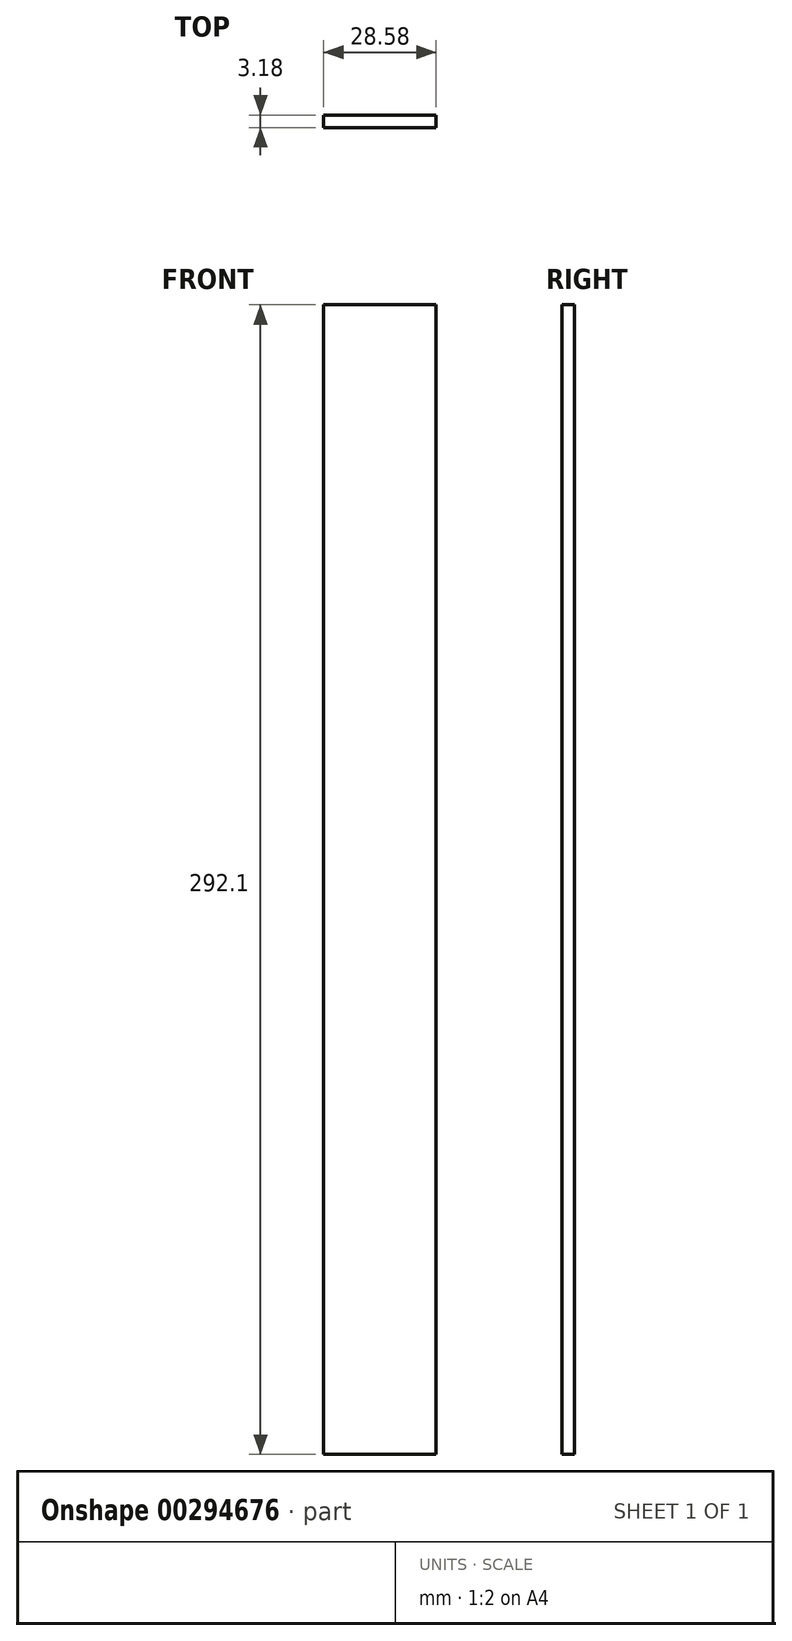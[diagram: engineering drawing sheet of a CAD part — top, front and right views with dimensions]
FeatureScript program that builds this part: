
annotation { "Feature Type Name" : "Feature", "Feature Type Description" : "" }
export const myFeature = defineFeature(function(context is Context, id is Id, definition is map)
    precondition{}
    {
        {
            var Q0;
            Q0=qCreatedBy(makeId("Front.planeOp"),FACE);
            var sketch = newSketch(context, id + "F0", { "sketchPlane" : qUnion([Q0])});
            skLineSegment(sketch, "E0.bottom", {"start": v(-14.29, 146.05) * mm, "end": v(14.29, 146.05) * mm});
            skLineSegment(sketch, "E0.top", {"start": v(-14.29, -146.05) * mm, "end": v(14.29, -146.05) * mm});
            skLineSegment(sketch, "E0.left", {"start": v(-14.29, 146.05) * mm, "end": v(-14.29, -146.05) * mm});
            skLineSegment(sketch, "E0.right", {"start": v(14.29, 146.05) * mm, "end": v(14.29, -146.05) * mm});
            skPoint(sketch, "E0.middle", {"position": v(0, 0) * mm});
            skSolve(sketch);
        }
        {
            var Q0;
            Q0=makeQuery(id+"F0.imprint","IMPRINT",FACE,{"disambiguationData":[TD([[makeQuery(id+"F0.imprint","IMPRINT",EDGE,{"derivedFrom":sQuery(id+"F0.wireOp",EDGE,"E0.bottom")}),-1.0]])]});
            extrude(context, id + "F1", {"entities" : qUnion([Q0]), "endBound" : BoundingType.SYMMETRIC, "depth" : 3.17 * mm});
        }
    });
